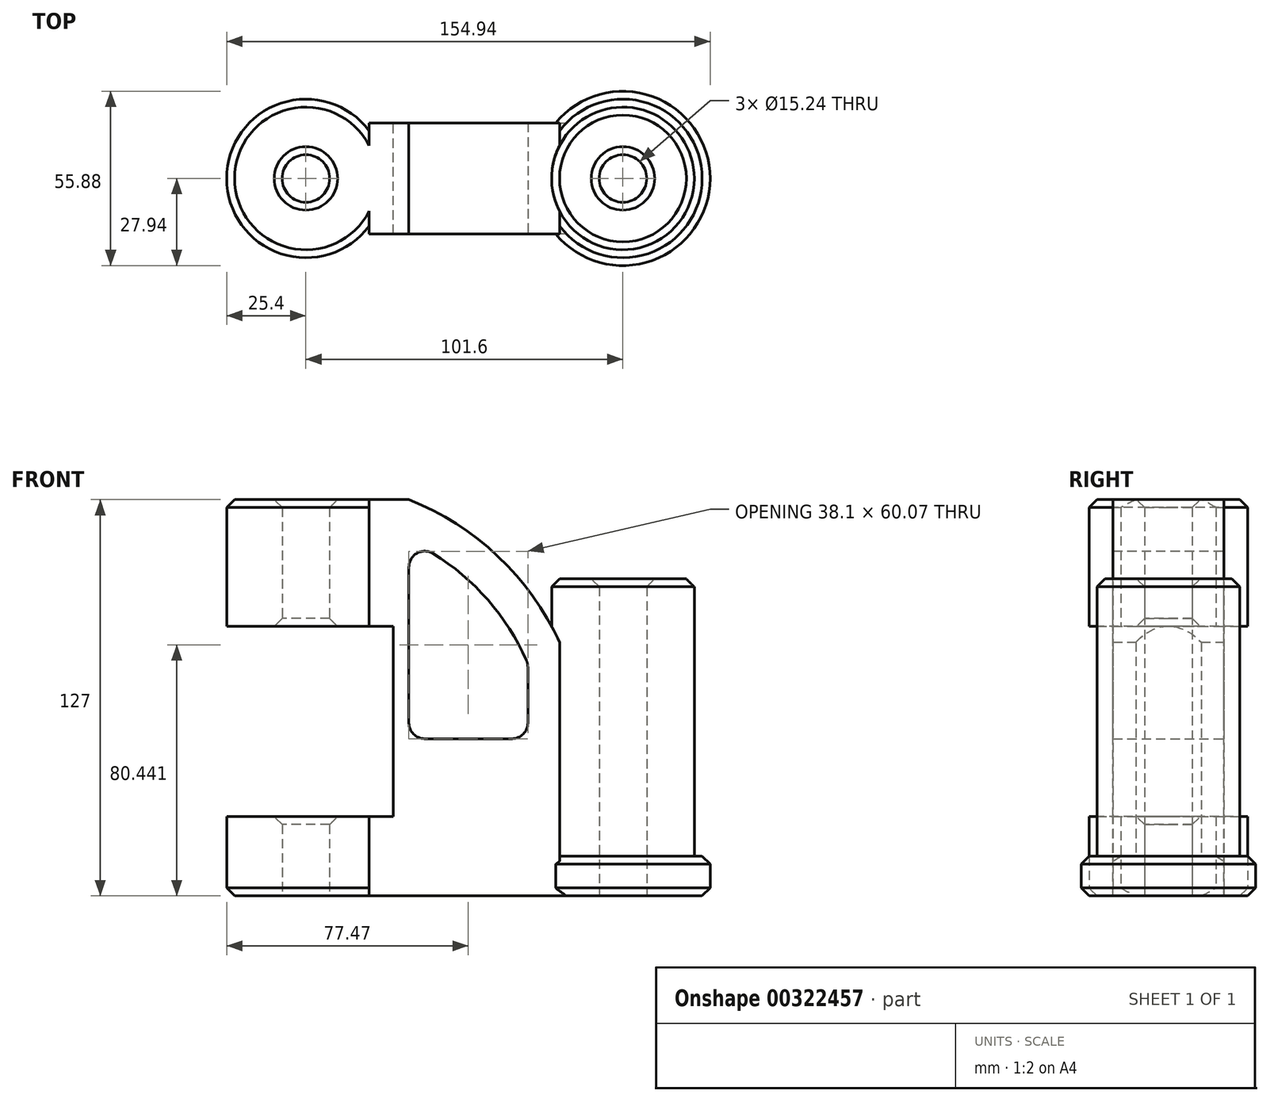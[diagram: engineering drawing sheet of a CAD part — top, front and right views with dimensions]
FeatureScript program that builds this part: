
annotation { "Feature Type Name" : "Feature", "Feature Type Description" : "" }
export const myFeature = defineFeature(function(context is Context, id is Id, definition is map)
    precondition{}
    {
        {
            var Q0;
            Q0=qCreatedBy(makeId("Top.planeOp"),FACE);
            var sketch = newSketch(context, id + "F0", { "sketchPlane" : qUnion([Q0])});
            skCircle(sketch, "E0", {"center": v(0, 0) * mm, "radius": 25.4 * mm});
            skCircle(sketch, "E1", {"center": v(0, 0) * mm, "radius": 7.62 * mm});
            skCircle(sketch, "E2", {"center": v(101.6, 0) * mm, "radius": 7.62 * mm});
            skCircle(sketch, "E3", {"center": v(101.6, 0) * mm, "radius": 22.86 * mm});
            skSolve(sketch);
        }
        {
            var Q0;
            Q0=makeQuery(id+"F0.imprint","IMPRINT",FACE,{"disambiguationData":[TD([[makeQuery(id+"F0.imprint","IMPRINT",EDGE,{"derivedFrom":sQuery(id+"F0.wireOp",EDGE,"E0")}),1.0]])]});
            extrude(context, id + "F1", {"entities" : qUnion([Q0]), "depth" : 127 * mm});
        }
        {
            var Q0;
            Q0=makeQuery(id+"F0.imprint","IMPRINT",FACE,{"disambiguationData":[TD([[makeQuery(id+"F0.imprint","IMPRINT",EDGE,{"derivedFrom":sQuery(id+"F0.wireOp",EDGE,"E2")}),-1.0]])]});
            extrude(context, id + "F2", {"entities" : qUnion([Q0]), "depth" : 101.6 * mm});
        }
        {
            var Q0;
            Q0=qCreatedBy(makeId("Front.planeOp"),FACE);
            var sketch = newSketch(context, id + "F3", { "sketchPlane" : qUnion([Q0])});
            skLineSegment(sketch, "E4", {"start": v(20.32, 0) * mm, "end": v(20.32, 127) * mm});
            skLineSegment(sketch, "E5", {"start": v(20.32, 127) * mm, "end": v(33.02, 127) * mm});
            skArc(sketch, "E6", {"start": v(81.28, 81.28) * mm, "mid": v(61.58, 108.82) * mm, "end": v(33.02, 127) * mm});
            skLineSegment(sketch, "E7", {"start": v(81.28, 81.28) * mm, "end": v(81.28, 0) * mm});
            skArc(sketch, "E8", {"start": v(33.02, 113.9) * mm, "mid": v(55.7, 97.71) * mm, "end": v(71.12, 74.5) * mm});
            skLineSegment(sketch, "E9", {"start": v(33.02, 113.9) * mm, "end": v(33.02, 50.4) * mm});
            skLineSegment(sketch, "E10", {"start": v(33.02, 50.4) * mm, "end": v(71.12, 50.4) * mm});
            skLineSegment(sketch, "E11", {"start": v(71.12, 50.4) * mm, "end": v(71.12, 74.5) * mm});
            skLineSegment(sketch, "E12", {"start": v(20.32, 0) * mm, "end": v(81.28, 0) * mm});
            skSolve(sketch);
        }
        {
            var Q0;
            Q0=makeQuery(id+"F3.imprint","IMPRINT",FACE,{"disambiguationData":[TD([[makeQuery(id+"F3.imprint","IMPRINT",EDGE,{"derivedFrom":sQuery(id+"F3.wireOp",EDGE,"E5")}),-1.0]])]});
            extrude(context, id + "F4", {"entities" : qUnion([Q0]), "operationType" : NewBodyOperationType.ADD, "depth" : 17.78 * mm, "hasSecondDirection" : true, "secondDirectionOppositeDirection" : true, "secondDirectionDepth" : 17.78 * mm});
        }
        {
            var Q0;
            Q0=qCreatedBy(makeId("Front.planeOp"),FACE);
            var sketch = newSketch(context, id + "F5", { "sketchPlane" : qUnion([Q0])});
            skLineSegment(sketch, "E13.bottom", {"start": v(-33.02, 86.36) * mm, "end": v(27.94, 86.36) * mm});
            skLineSegment(sketch, "E13.top", {"start": v(-33.02, 25.4) * mm, "end": v(27.94, 25.4) * mm});
            skLineSegment(sketch, "E13.left", {"start": v(-33.02, 86.36) * mm, "end": v(-33.02, 25.4) * mm});
            skLineSegment(sketch, "E13.right", {"start": v(27.94, 86.36) * mm, "end": v(27.94, 25.4) * mm});
            skSolve(sketch);
        }
        {
            var Q0;
            Q0=makeQuery(id+"F5.imprint","IMPRINT",FACE,{"disambiguationData":[TD([[makeQuery(id+"F5.imprint","IMPRINT",EDGE,{"derivedFrom":sQuery(id+"F5.wireOp",EDGE,"E13.bottom")}),-1.0]])]});
            extrude(context, id + "F6", {"entities" : qUnion([Q0]), "operationType" : NewBodyOperationType.REMOVE, "depth" : 25.4 * mm, "hasSecondDirection" : true, "secondDirectionOppositeDirection" : true, "secondDirectionDepth" : 25.4 * mm});
        }
        {
            var Q0;
            Q0=makeQuery(id+"F4.opExtrude","SWEPT_EDGE",EDGE,{"disambiguationData":[OSD([sQuery(id+"F3.wireOp",EDGE,"E8"),sQuery(id+"F3.wireOp",EDGE,"E9")])]});
            var Q1;
            Q1=makeQuery(id+"F4.opExtrude","SWEPT_EDGE",EDGE,{"disambiguationData":[OSD([sQuery(id+"F3.wireOp",EDGE,"E9"),sQuery(id+"F3.wireOp",EDGE,"E10")])]});
            var Q2;
            Q2=makeQuery(id+"F4.opExtrude","SWEPT_EDGE",EDGE,{"disambiguationData":[OSD([sQuery(id+"F3.wireOp",EDGE,"E10"),sQuery(id+"F3.wireOp",EDGE,"E11")])]});
            var Q3;
            Q3=makeQuery(id+"F4.opExtrude","SWEPT_EDGE",EDGE,{"disambiguationData":[OSD([sQuery(id+"F3.wireOp",EDGE,"E8"),sQuery(id+"F3.wireOp",EDGE,"E11")])]});
            fillet(context, id + "F7", {"entities" : qUnion([Q0, Q1, Q2, Q3]), "radius" : 5.08 * mm, "tangentPropagation" : true, "allowEdgeOverflow" : false});
        }
        {
            var Q0;
            Q0=makeQuery(id+"F1.opExtrude","CAP_EDGE",EDGE,{"disambiguationData":[OSD([sQuery(id+"F0.wireOp",EDGE,"E0")])],"isStart":true});
            var Q1;
            Q1=makeQuery(id+"F6.boolean.opBoolean","INTERSECT",EDGE,{"derivedFrom":[makeQuery(id+"F1.opExtrude","SWEPT_FACE",FACE,{"disambiguationData":[OSD([sQuery(id+"F0.wireOp",EDGE,"E1")])]}),makeQuery(id+"F6.opExtrude","SWEPT_FACE",FACE,{"disambiguationData":[OSD([sQuery(id+"F5.wireOp",EDGE,"E13.top")])]})]});
            var Q2;
            Q2=makeQuery(id+"F6.boolean.opBoolean","INTERSECT",EDGE,{"derivedFrom":[makeQuery(id+"F1.opExtrude","SWEPT_FACE",FACE,{"disambiguationData":[OSD([sQuery(id+"F0.wireOp",EDGE,"E1")])]}),makeQuery(id+"F6.opExtrude","SWEPT_FACE",FACE,{"disambiguationData":[OSD([sQuery(id+"F5.wireOp",EDGE,"E13.bottom")])]})]});
            var Q3;
            Q3=makeQuery(id+"F1.opExtrude","CAP_EDGE",EDGE,{"disambiguationData":[OSD([sQuery(id+"F0.wireOp",EDGE,"E0")])],"isStart":false});
            chamfer(context, id + "F8", {"entities" : qUnion([Q0, Q1, Q2, Q3]), "width" : 2.54 * mm, "tangentPropagation" : true});
        }
        {
            var Q0;
            Q0=qCreatedBy(makeId("Top.planeOp"),FACE);
            var sketch = newSketch(context, id + "F9", { "sketchPlane" : qUnion([Q0])});
            skCircle(sketch, "E14.0.0", {"center": v(101.6, 0) * mm, "radius": 22.86 * mm});
            skCircle(sketch, "E15", {"center": v(101.6, 0) * mm, "radius": 27.94 * mm});
            skSolve(sketch);
        }
        {
            var Q0;
            Q0=makeQuery(id+"F9.imprint","IMPRINT",FACE,{"disambiguationData":[TD([[makeQuery(id+"F9.imprint","IMPRINT",EDGE,{"derivedFrom":sQuery(id+"F9.wireOp",EDGE,"E14.0.0")}),-1.0]])]});
            extrude(context, id + "F10", {"entities" : qUnion([Q0]), "operationType" : NewBodyOperationType.ADD, "depth" : 12.7 * mm});
        }
        {
            var Q0;
            Q0=makeQuery(id+"F10.opExtrude","CAP_EDGE",EDGE,{"disambiguationData":[OSD([sQuery(id+"F9.wireOp",EDGE,"E15")])],"isStart":true});
            var Q1;
            Q1=makeQuery(id+"F10.opExtrude","CAP_EDGE",EDGE,{"disambiguationData":[OSD([sQuery(id+"F9.wireOp",EDGE,"E15")])],"isStart":false});
            var Q2;
            Q2=makeQuery(id+"F2.opExtrude","CAP_EDGE",EDGE,{"disambiguationData":[OSD([sQuery(id+"F0.wireOp",EDGE,"E3")])],"isStart":false});
            var Q3;
            Q3=makeQuery(id+"F2.opExtrude","CAP_EDGE",EDGE,{"disambiguationData":[OSD([sQuery(id+"F0.wireOp",EDGE,"E2")])],"isStart":false});
            var Q4;
            Q4=makeQuery(id+"F1.opExtrude","CAP_EDGE",EDGE,{"disambiguationData":[OSD([sQuery(id+"F0.wireOp",EDGE,"E1")])],"isStart":false});
            chamfer(context, id + "F11", {"entities" : qUnion([Q0, Q1, Q2, Q3, Q4]), "width" : 2.54 * mm, "tangentPropagation" : true});
        }
    });
